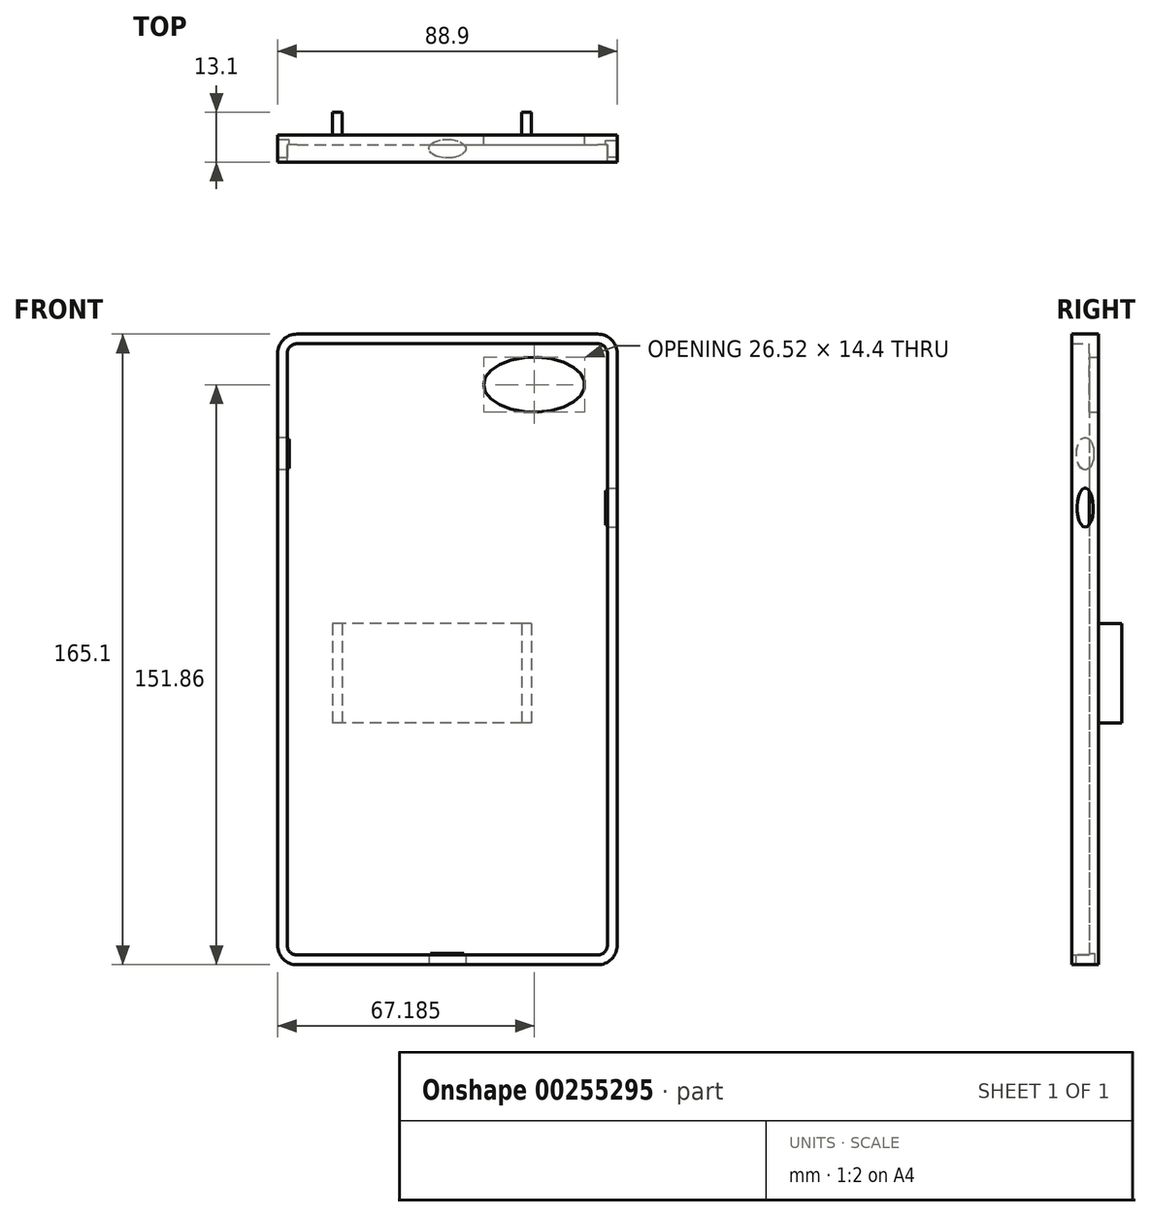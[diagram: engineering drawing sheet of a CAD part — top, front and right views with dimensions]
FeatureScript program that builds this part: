
annotation { "Feature Type Name" : "Feature", "Feature Type Description" : "" }
export const myFeature = defineFeature(function(context is Context, id is Id, definition is map)
    precondition{}
    {
        {
            var Q0;
            Q0=qCreatedBy(makeId("Front.planeOp"),FACE);
            var sketch = newSketch(context, id + "F0", { "sketchPlane" : qUnion([Q0])});
            skLineSegment(sketch, "E0.bottom", {"start": v(-44.45, 82.55) * mm, "end": v(44.45, 82.55) * mm});
            skLineSegment(sketch, "E0.top", {"start": v(-44.45, -82.55) * mm, "end": v(44.45, -82.55) * mm});
            skLineSegment(sketch, "E0.left", {"start": v(-44.45, 82.55) * mm, "end": v(-44.45, -82.55) * mm});
            skLineSegment(sketch, "E0.right", {"start": v(44.45, 82.55) * mm, "end": v(44.45, -82.55) * mm});
            skPoint(sketch, "E0.middle", {"position": v(0, 0) * mm});
            skSolve(sketch);
        }
        {
            var Q0;
            Q0=makeQuery(id+"F0.imprint","IMPRINT",FACE,{"disambiguationData":[TD([[makeQuery(id+"F0.imprint","IMPRINT",EDGE,{"derivedFrom":sQuery(id+"F0.wireOp",EDGE,"E0.bottom")}),-1.0]])]});
            extrude(context, id + "F1", {"entities" : qUnion([Q0]), "endBound" : BoundingType.SYMMETRIC, "depth" : 7.1 * mm});
        }
        {
            var Q0;
            Q0=makeQuery(id+"F1.opExtrude","SWEPT_EDGE",EDGE,{"disambiguationData":[OSD([sQuery(id+"F0.wireOp",EDGE,"E0.bottom"),sQuery(id+"F0.wireOp",EDGE,"E0.left")])]});
            var Q1;
            Q1=makeQuery(id+"F1.opExtrude","SWEPT_EDGE",EDGE,{"disambiguationData":[OSD([sQuery(id+"F0.wireOp",EDGE,"E0.bottom"),sQuery(id+"F0.wireOp",EDGE,"E0.right")])]});
            var Q2;
            Q2=makeQuery(id+"F1.opExtrude","SWEPT_EDGE",EDGE,{"disambiguationData":[OSD([sQuery(id+"F0.wireOp",EDGE,"E0.top"),sQuery(id+"F0.wireOp",EDGE,"E0.right")])]});
            var Q3;
            Q3=makeQuery(id+"F1.opExtrude","SWEPT_EDGE",EDGE,{"disambiguationData":[OSD([sQuery(id+"F0.wireOp",EDGE,"E0.top"),sQuery(id+"F0.wireOp",EDGE,"E0.left")])]});
            fillet(context, id + "F2", {"entities" : qUnion([Q0, Q1, Q2, Q3]), "radius" : 5.08 * mm, "tangentPropagation" : true, "allowEdgeOverflow" : false});
        }
        {
            var Q0;
            Q0=makeQuery(id+"F1.opExtrude","CAP_FACE",FACE,{"disambiguationData":[OSD([sQuery(id+"F0.wireOp",EDGE,"E0.bottom"),sQuery(id+"F0.wireOp",EDGE,"E0.top"),sQuery(id+"F0.wireOp",EDGE,"E0.left"),sQuery(id+"F0.wireOp",EDGE,"E0.right")])],"isStart":false});
            shell(context, id + "F3", {"entities" : qUnion([Q0]), "thickness" : 2.54 * mm});
        }
        {
            var Q0;
            Q0=makeQuery(id+"F3.opShell","OFFSET_FACE",FACE,{"disambiguationData":[OSD([sQuery(id+"F0.wireOp",EDGE,"E0.bottom"),sQuery(id+"F0.wireOp",EDGE,"E0.top"),sQuery(id+"F0.wireOp",EDGE,"E0.left"),sQuery(id+"F0.wireOp",EDGE,"E0.right")])]});
            var sketch = newSketch(context, id + "F4", { "sketchPlane" : qUnion([Q0])});
            skEllipse(sketch, "E1", {"center": v(22.74, 69.31) * mm, "majorRadius": 13.26 * mm, "minorRadius": 7.2 * mm, "majorAxis": v(-1, 0)});
            skSolve(sketch);
        }
        {
            var Q0;
            Q0=makeQuery(id+"F4.imprint","IMPRINT",FACE,{"disambiguationData":[TD([[makeQuery(id+"F4.imprint","IMPRINT",EDGE,{"derivedFrom":sQuery(id+"F4.wireOp",EDGE,"E1")}),1.0]])]});
            var Q1;
            Q1=sQuery(id+"F4.wireOp",EDGE,"x5JoyBv7-c6Nn-HsqA-Argo-8u5VR9NVX8vm");
            extrude(context, id + "F5", {"entities" : qUnion([Q0]), "operationType" : NewBodyOperationType.REMOVE, "surfaceEntities" : qUnion([Q1]), "endBound" : BoundingType.SYMMETRIC, "depth" : 25 * mm});
        }
        {
            var Q0;
            Q0=makeQuery(id+"F1.opExtrude","SWEPT_FACE",FACE,{"disambiguationData":[OSD([sQuery(id+"F0.wireOp",EDGE,"E0.top")])]});
            var sketch = newSketch(context, id + "F6", { "sketchPlane" : qUnion([Q0])});
            skEllipse(sketch, "E2", {"center": v(0, 0) * mm, "majorRadius": 4.82 * mm, "minorRadius": 2.45 * mm, "majorAxis": v(-1, 0)});
            skLineSegment(sketch, "E3.bottom", {"start": v(-26.47, 1.64) * mm, "end": v(-7.45, 1.64) * mm});
            skLineSegment(sketch, "E3.top", {"start": v(-26.47, -2.35) * mm, "end": v(-7.45, -2.35) * mm});
            skLineSegment(sketch, "E3.left", {"start": v(-26.47, 1.64) * mm, "end": v(-26.47, -2.35) * mm});
            skLineSegment(sketch, "E3.right", {"start": v(-7.45, 1.64) * mm, "end": v(-7.45, -2.35) * mm});
            skLineSegment(sketch, "E4.bottom", {"start": v(7.31, 1.9) * mm, "end": v(26.47, 1.9) * mm});
            skLineSegment(sketch, "E4.top", {"start": v(7.31, -2.09) * mm, "end": v(26.47, -2.09) * mm});
            skLineSegment(sketch, "E4.left", {"start": v(7.31, 1.9) * mm, "end": v(7.31, -2.09) * mm});
            skLineSegment(sketch, "E4.right", {"start": v(26.47, 1.9) * mm, "end": v(26.47, -2.09) * mm});
            skSolve(sketch);
        }
        {
            var Q0;
            Q0=makeQuery(id+"F6.imprint","IMPRINT",FACE,{"disambiguationData":[TD([[makeQuery(id+"F6.imprint","IMPRINT",EDGE,{"derivedFrom":sQuery(id+"F6.wireOp",EDGE,"E2")}),1.0]])]});
            extrude(context, id + "F7", {"entities" : qUnion([Q0]), "operationType" : NewBodyOperationType.REMOVE, "oppositeDirection" : true, "depth" : 3 * mm});
        }
        {
            var Q0;
            Q0=makeQuery(id+"F1.opExtrude","SWEPT_FACE",FACE,{"disambiguationData":[OSD([sQuery(id+"F0.wireOp",EDGE,"E0.left")])]});
            var sketch = newSketch(context, id + "F8", { "sketchPlane" : qUnion([Q0])});
            skEllipse(sketch, "E5", {"center": v(0, 51.27) * mm, "majorRadius": 4.25 * mm, "minorRadius": 2.28 * mm, "majorAxis": v(0, -1)});
            skSolve(sketch);
        }
        {
            var Q0;
            Q0 = qSketchRegion(id + "F8", true);
            extrude(context, id + "F9", {"entities" : qUnion([Q0]), "operationType" : NewBodyOperationType.REMOVE, "oppositeDirection" : true, "depth" : 3 * mm});
        }
        {
            var Q0;
            Q0=makeQuery(id+"F1.opExtrude","SWEPT_FACE",FACE,{"disambiguationData":[OSD([sQuery(id+"F0.wireOp",EDGE,"E0.right")])]});
            var sketch = newSketch(context, id + "F10", { "sketchPlane" : qUnion([Q0])});
            skEllipse(sketch, "E6", {"center": v(0, 37.1) * mm, "majorRadius": 5.1 * mm, "minorRadius": 2.15 * mm, "majorAxis": v(0, -1)});
            skSolve(sketch);
        }
        {
            var Q0;
            Q0 = qSketchRegion(id + "F10", true);
            extrude(context, id + "F11", {"entities" : qUnion([Q0]), "operationType" : NewBodyOperationType.REMOVE, "oppositeDirection" : true, "depth" : 3 * mm});
        }
        {
            var Q0;
            Q0=makeQuery(id+"F1.opExtrude","CAP_FACE",FACE,{"disambiguationData":[OSD([sQuery(id+"F0.wireOp",EDGE,"E0.bottom"),sQuery(id+"F0.wireOp",EDGE,"E0.top"),sQuery(id+"F0.wireOp",EDGE,"E0.left"),sQuery(id+"F0.wireOp",EDGE,"E0.right")])],"isStart":true});
            var sketch = newSketch(context, id + "F12", { "sketchPlane" : qUnion([Q0])});
            skLineSegment(sketch, "E7.bottom", {"start": v(-21.98, 6.78) * mm, "end": v(30.02, 6.78) * mm});
            skLineSegment(sketch, "E7.top", {"start": v(-21.98, -19.22) * mm, "end": v(30.02, -19.22) * mm});
            skLineSegment(sketch, "E7.left", {"start": v(-21.98, 6.78) * mm, "end": v(-21.98, -19.22) * mm});
            skLineSegment(sketch, "E7.right", {"start": v(30.02, 6.78) * mm, "end": v(30.02, -19.22) * mm});
            skSolve(sketch);
        }
        {
            var Q0;
            Q0=makeQuery(id+"F12.imprint","IMPRINT",FACE,{"disambiguationData":[TD([[makeQuery(id+"F12.imprint","IMPRINT",EDGE,{"derivedFrom":sQuery(id+"F12.wireOp",EDGE,"E7.bottom")}),-1.0]])]});
            extrude(context, id + "F13", {"entities" : qUnion([Q0]), "operationType" : NewBodyOperationType.ADD, "depth" : 6 * mm});
        }
        {
            var Q0;
            Q0=makeQuery(id+"F13.opExtrude","CAP_FACE",FACE,{"disambiguationData":[OSD([sQuery(id+"F12.wireOp",EDGE,"E7.bottom"),sQuery(id+"F12.wireOp",EDGE,"E7.top"),sQuery(id+"F12.wireOp",EDGE,"E7.left"),sQuery(id+"F12.wireOp",EDGE,"E7.right")])],"isStart":false});
            var Q1;
            Q1=makeQuery(id+"F13.opExtrude","SWEPT_FACE",FACE,{"disambiguationData":[OSD([sQuery(id+"F12.wireOp",EDGE,"E7.top")])]});
            var Q2;
            Q2=makeQuery(id+"F13.opExtrude","SWEPT_FACE",FACE,{"disambiguationData":[OSD([sQuery(id+"F12.wireOp",EDGE,"E7.bottom")])]});
            shell(context, id + "F14", {"entities" : qUnion([Q0, Q1, Q2]), "thickness" : 2.5 * mm});
        }
    });
